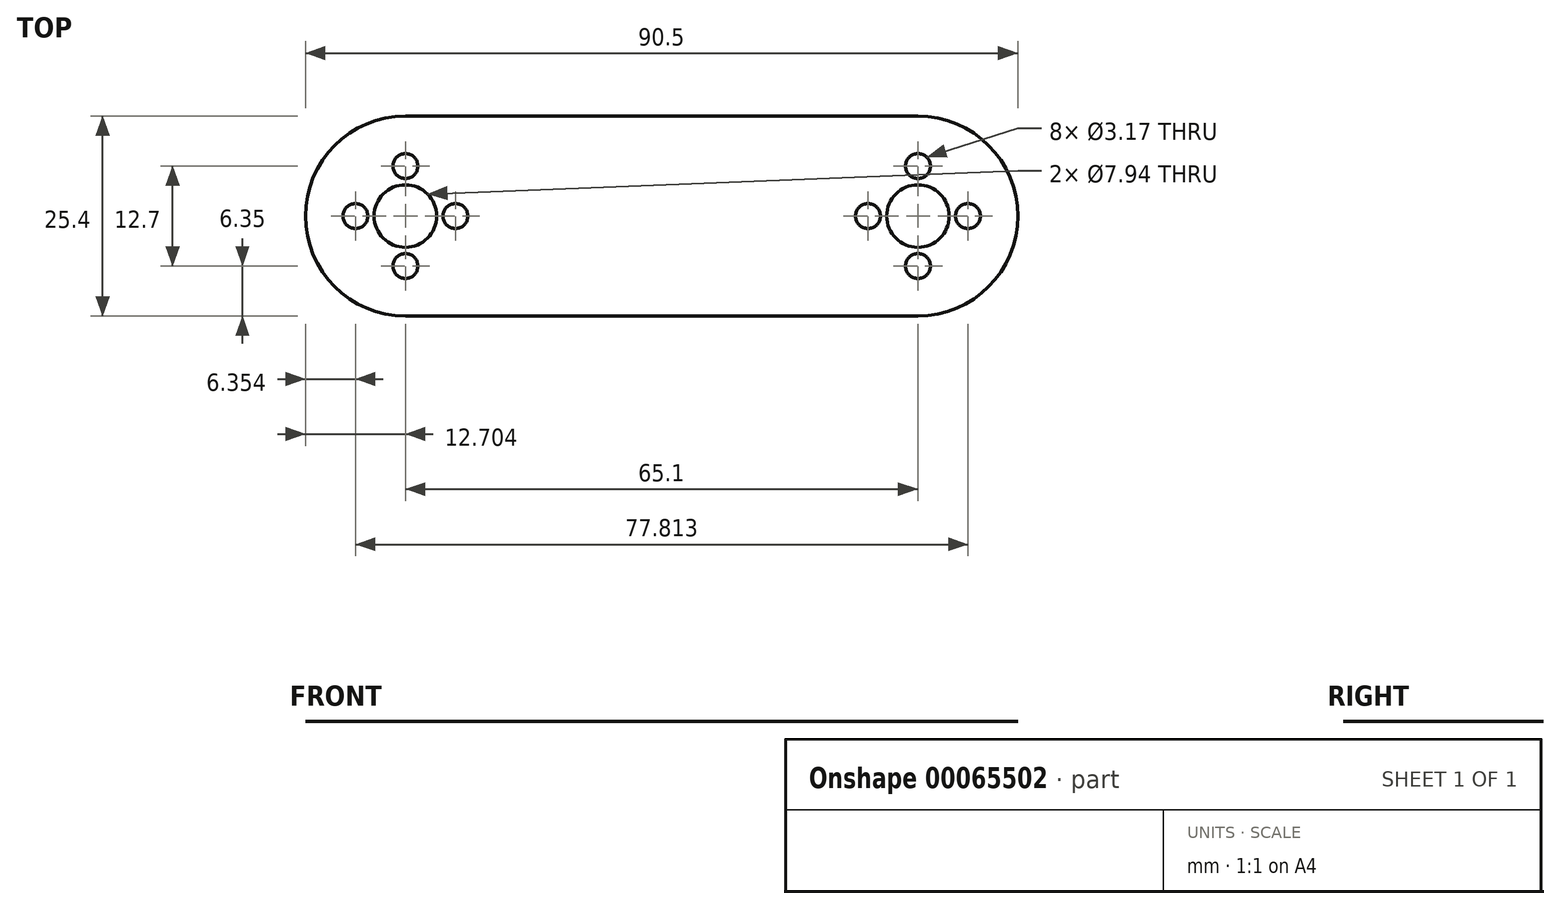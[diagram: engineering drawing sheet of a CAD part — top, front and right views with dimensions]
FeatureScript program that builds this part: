
annotation { "Feature Type Name" : "Feature", "Feature Type Description" : "" }
export const myFeature = defineFeature(function(context is Context, id is Id, definition is map)
    precondition{}
    {
        {
            var Q0;
            Q0=qCreatedBy(makeId("Top.planeOp"),FACE);
            var sketch = newSketch(context, id + "F0", { "sketchPlane" : qUnion([Q0])});
            skLineSegment(sketch, "E0", {"start": v(-32.56, 0) * mm, "end": v(0, 0) * mm});
            skLineSegment(sketch, "E1", {"start": v(0, 0) * mm, "end": v(32.54, 0) * mm});
            skArc(sketch, "E2", {"start": v(-32.56, 12.7) * mm, "mid": v(-45.26, 0) * mm, "end": v(-32.56, -12.7) * mm});
            skArc(sketch, "E3", {"start": v(32.54, 12.7) * mm, "mid": v(45.24, 0) * mm, "end": v(32.54, -12.7) * mm});
            skLineSegment(sketch, "E4", {"start": v(-32.56, 12.7) * mm, "end": v(32.54, 12.7) * mm});
            skLineSegment(sketch, "E5", {"start": v(-32.56, -12.7) * mm, "end": v(32.54, -12.7) * mm});
            skCircle(sketch, "E6", {"center": v(-32.56, 0) * mm, "radius": 3.97 * mm});
            skCircle(sketch, "E7", {"center": v(32.54, 0) * mm, "radius": 3.97 * mm});
            skLineSegment(sketch, "E8", {"start": v(-32.56, 0) * mm, "end": v(-32.56, 6.35) * mm});
            skLineSegment(sketch, "E9", {"start": v(-32.56, 6.35) * mm, "end": v(-32.56, 0) * mm});
            skLineSegment(sketch, "E10", {"start": v(-32.56, 0) * mm, "end": v(-32.56, -6.35) * mm});
            skLineSegment(sketch, "E11", {"start": v(-32.56, 0) * mm, "end": v(-38.9, 0) * mm});
            skLineSegment(sketch, "E12", {"start": v(-32.56, 0) * mm, "end": v(-26.2, 0) * mm});
            skCircle(sketch, "E13", {"center": v(-32.56, 6.35) * mm, "radius": 1.59 * mm});
            skCircle(sketch, "E14", {"center": v(-38.9, 0) * mm, "radius": 1.59 * mm});
            skCircle(sketch, "E15", {"center": v(-32.56, -6.35) * mm, "radius": 1.59 * mm});
            skCircle(sketch, "E16", {"center": v(-26.2, 0) * mm, "radius": 1.59 * mm});
            skLineSegment(sketch, "E17", {"start": v(0, 12.7) * mm, "end": v(0, -12.7) * mm});
            skCircle(sketch, "E18.MirrorC", {"center": v(32.56, 6.35) * mm, "radius": 1.59 * mm});
            skCircle(sketch, "E19.MirrorC", {"center": v(38.9, 0) * mm, "radius": 1.59 * mm});
            skCircle(sketch, "E20.MirrorC", {"center": v(32.56, -6.35) * mm, "radius": 1.59 * mm});
            skCircle(sketch, "E21.MirrorC", {"center": v(26.2, 0) * mm, "radius": 1.59 * mm});
            skSolve(sketch);
        }
        {
            var Q0;
            Q0 = qSketchRegion(id + "F0", true);
            extrude(context, id + "F1", {"entities" : qUnion([Q0]), "depth" : 3 / 812.8 * mm});
        }
    });
